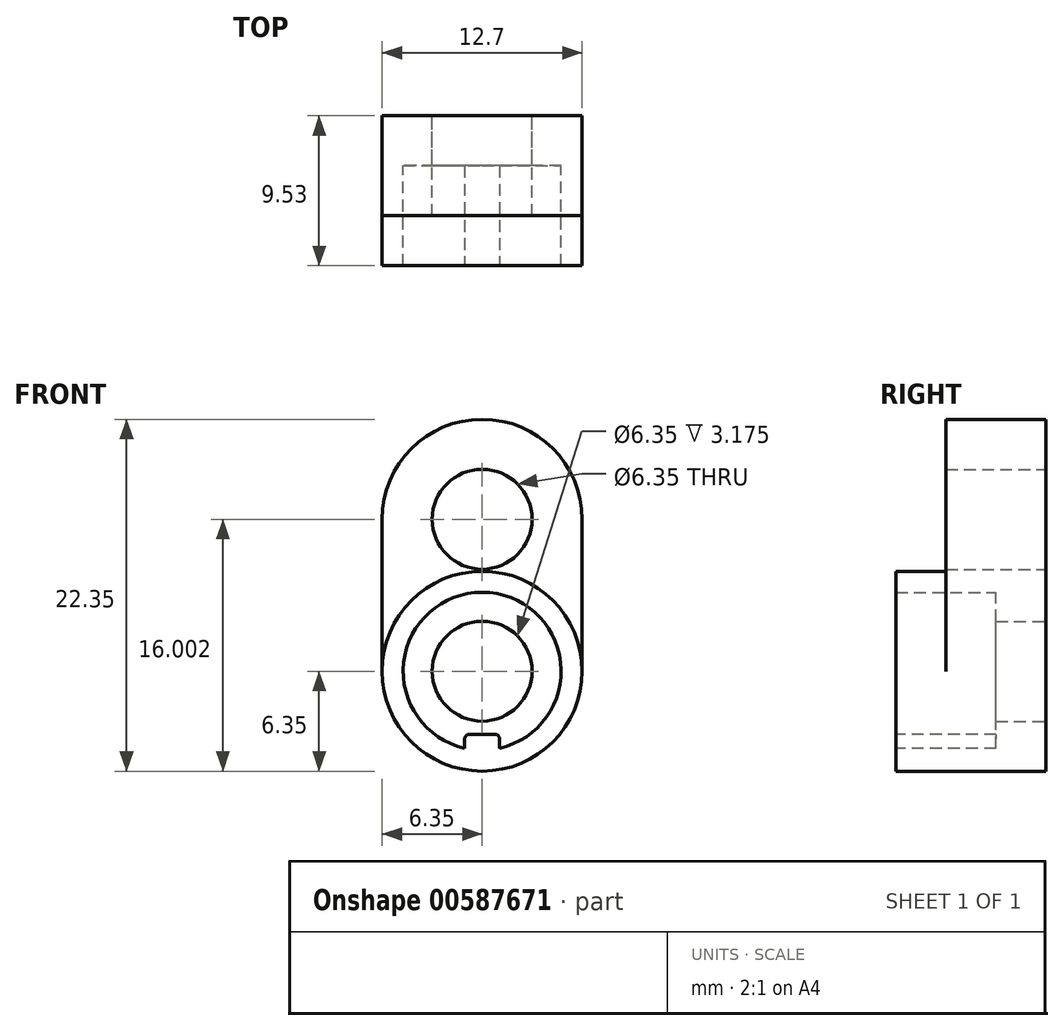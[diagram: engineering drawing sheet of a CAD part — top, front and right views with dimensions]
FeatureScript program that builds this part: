
annotation { "Feature Type Name" : "Feature", "Feature Type Description" : "" }
export const myFeature = defineFeature(function(context is Context, id is Id, definition is map)
    precondition{}
    {
        {
            var Q0;
            Q0=qCreatedBy(makeId("Front.planeOp"),FACE);
            var sketch = newSketch(context, id + "F0", { "sketchPlane" : qUnion([Q0])});
            skCircle(sketch, "E0", {"center": v(0, 0) * mm, "radius": 3.18 * mm});
            skCircle(sketch, "E1", {"center": v(0, 0) * mm, "radius": 6.35 * mm});
            skSolve(sketch);
        }
        {
            var Q0;
            Q0 = qSketchRegion(id + "F0", true);
            extrude(context, id + "F1", {"entities" : qUnion([Q0]), "depth" : 3.17 * mm, "offsetDistance" : 25.4 * mm});
        }
        {
            var Q0;
            Q0=makeQuery(id+"F1.opExtrude","CAP_FACE",FACE,{"disambiguationData":[OSD([sQuery(id+"F0.wireOp",EDGE,"E0"),sQuery(id+"F0.wireOp",EDGE,"E1")])],"isStart":false});
            var sketch = newSketch(context, id + "F2", { "sketchPlane" : qUnion([Q0])});
            skCircle(sketch, "E2", {"center": v(0, 0) * mm, "radius": 5.02 * mm});
            skCircle(sketch, "E3.0", {"center": v(0, 0) * mm, "radius": 6.35 * mm});
            skSolve(sketch);
        }
        {
            var Q0;
            Q0 = qSketchRegion(id + "F2", true);
            extrude(context, id + "F3", {"entities" : qUnion([Q0]), "operationType" : NewBodyOperationType.ADD, "depth" : 6.35 * mm, "offsetDistance" : 25.4 * mm});
        }
        {
            var Q0;
            Q0=makeQuery(id+"F1.opExtrude","CAP_FACE",FACE,{"disambiguationData":[OSD([sQuery(id+"F0.wireOp",EDGE,"E0"),sQuery(id+"F0.wireOp",EDGE,"E1")])],"isStart":true});
            var sketch = newSketch(context, id + "F4", { "sketchPlane" : qUnion([Q0])});
            skLineSegment(sketch, "E4", {"start": v(0, 0) * mm, "end": v(0, 9.65) * mm, "construction": true});
            skCircle(sketch, "E5", {"center": v(0, 9.65) * mm, "radius": 3.18 * mm});
            skCircle(sketch, "E6.0", {"center": v(0, 0) * mm, "radius": 6.35 * mm});
            skLineSegment(sketch, "E7", {"start": v(-6.35, 0) * mm, "end": v(-6.35, 9.65) * mm});
            skLineSegment(sketch, "E8", {"start": v(6.35, 0) * mm, "end": v(6.35, 9.65) * mm});
            skLineSegment(sketch, "E9", {"start": v(0, 9.65) * mm, "end": v(0, 9.65) * mm});
            skCircle(sketch, "E10", {"center": v(0, 9.65) * mm, "radius": 6.35 * mm});
            skLineSegment(sketch, "E11", {"start": v(-6.35, 9.65) * mm, "end": v(0, 9.65) * mm, "construction": true});
            skLineSegment(sketch, "E12", {"start": v(0, 9.65) * mm, "end": v(6.35, 9.65) * mm, "construction": true});
            skSolve(sketch);
        }
        {
            var Q0;
            {var subQ1=sQuery(id+"F4.wireOp",EDGE,"gx27LyLz-Ukwh-S3wJ-jbhg-FnkPYNk82Kv1");Q0=makeQuery(id+"F4.imprint","IMPRINT",FACE,{"disambiguationData":[TD([[makeQuery(id+"F4.imprint","IMPRINT",EDGE,{"derivedFrom":subQ1}),-1.0]])]});}
            var Q1;
            Q1=makeQuery(id+"F4.imprint","IMPRINT",FACE,{"disambiguationData":[TD([[makeQuery(id+"F4.imprint","IMPRINT",EDGE,{"derivedFrom":sQuery(id+"F4.wireOp",EDGE,"E5")}),-1.0]])]});
            var Q2;
            {var subQ0=sQuery(id+"F4.wireOp",EDGE,"E7");Q2=makeQuery(id+"F4.imprint","IMPRINT",FACE,{"disambiguationData":[TD([[makeQuery(id+"F4.imprint","IMPRINT",EDGE,{"derivedFrom":subQ0}),-1.0]])]});}
            var Q3;
            {var subQ0=sQuery(id+"F4.wireOp",EDGE,"E8");Q3=makeQuery(id+"F4.imprint","IMPRINT",FACE,{"disambiguationData":[TD([[makeQuery(id+"F4.imprint","IMPRINT",EDGE,{"derivedFrom":subQ0}),1.0]])]});}
            extrude(context, id + "F5", {"entities" : qUnion([Q0, Q1, Q2, Q3]), "operationType" : NewBodyOperationType.ADD, "oppositeDirection" : true, "depth" : 6.35 * mm, "offsetDistance" : 25.4 * mm});
        }
        {
            var Q0;
            Q0=makeQuery(id+"F3.opExtrude","CAP_FACE",FACE,{"disambiguationData":[OSD([sQuery(id+"F2.wireOp",EDGE,"E2"),sQuery(id+"F2.wireOp",EDGE,"E3.0")])],"isStart":false});
            var sketch = newSketch(context, id + "F6", { "sketchPlane" : qUnion([Q0])});
            skLineSegment(sketch, "E13", {"start": v(0, 0) * mm, "end": v(0, -5.02) * mm, "construction": true});
            skArc(sketch, "E14.0", {"start": v(-1.1, -4.9) * mm, "mid": v(0, -5.02) * mm, "end": v(1.1, -4.9) * mm});
            skLineSegment(sketch, "E15", {"start": v(-1.1, -4) * mm, "end": v(-1.1, -4.9) * mm});
            skLineSegment(sketch, "E16", {"start": v(1.1, -4) * mm, "end": v(1.1, -4.9) * mm});
            skLineSegment(sketch, "E17", {"start": v(-1.1, -4) * mm, "end": v(1.1, -4) * mm});
            skLineSegment(sketch, "E18", {"start": v(-1.1, -4.9) * mm, "end": v(0, -4.9) * mm, "construction": true});
            skLineSegment(sketch, "E19", {"start": v(0, -4.9) * mm, "end": v(1.1, -4.9) * mm, "construction": true});
            skSolve(sketch);
        }
        {
            var Q0;
            Q0 = qSketchRegion(id + "F6", true);
            var Q1;
            Q1=makeQuery(id+"F1.opExtrude","CAP_FACE",FACE,{"disambiguationData":[OSD([sQuery(id+"F0.wireOp",EDGE,"E0"),sQuery(id+"F0.wireOp",EDGE,"E1")])],"isStart":false});
            extrude(context, id + "F7", {"entities" : qUnion([Q0]), "operationType" : NewBodyOperationType.ADD, "endBound" : BoundingType.UP_TO_SURFACE, "oppositeDirection" : true, "depth" : 25.4 * mm, "endBoundEntityFace" : qUnion([Q1]), "offsetDistance" : 25.4 * mm});
        }
        {
            var Q0;
            Q0=makeQuery(id+"F7.opExtrude","SWEPT_EDGE",EDGE,{"disambiguationData":[OSD([sQuery(id+"F6.wireOp",EDGE,"E16"),sQuery(id+"F6.wireOp",EDGE,"E17")])]});
            var Q1;
            Q1=makeQuery(id+"F7.opExtrude","SWEPT_EDGE",EDGE,{"disambiguationData":[OSD([sQuery(id+"F6.wireOp",EDGE,"E15"),sQuery(id+"F6.wireOp",EDGE,"E17")])]});
            fillet(context, id + "F8", {"entities" : qUnion([Q0, Q1]), "radius" : 0.3 * mm, "tangentPropagation" : true, "allowEdgeOverflow" : false});
        }
    });
